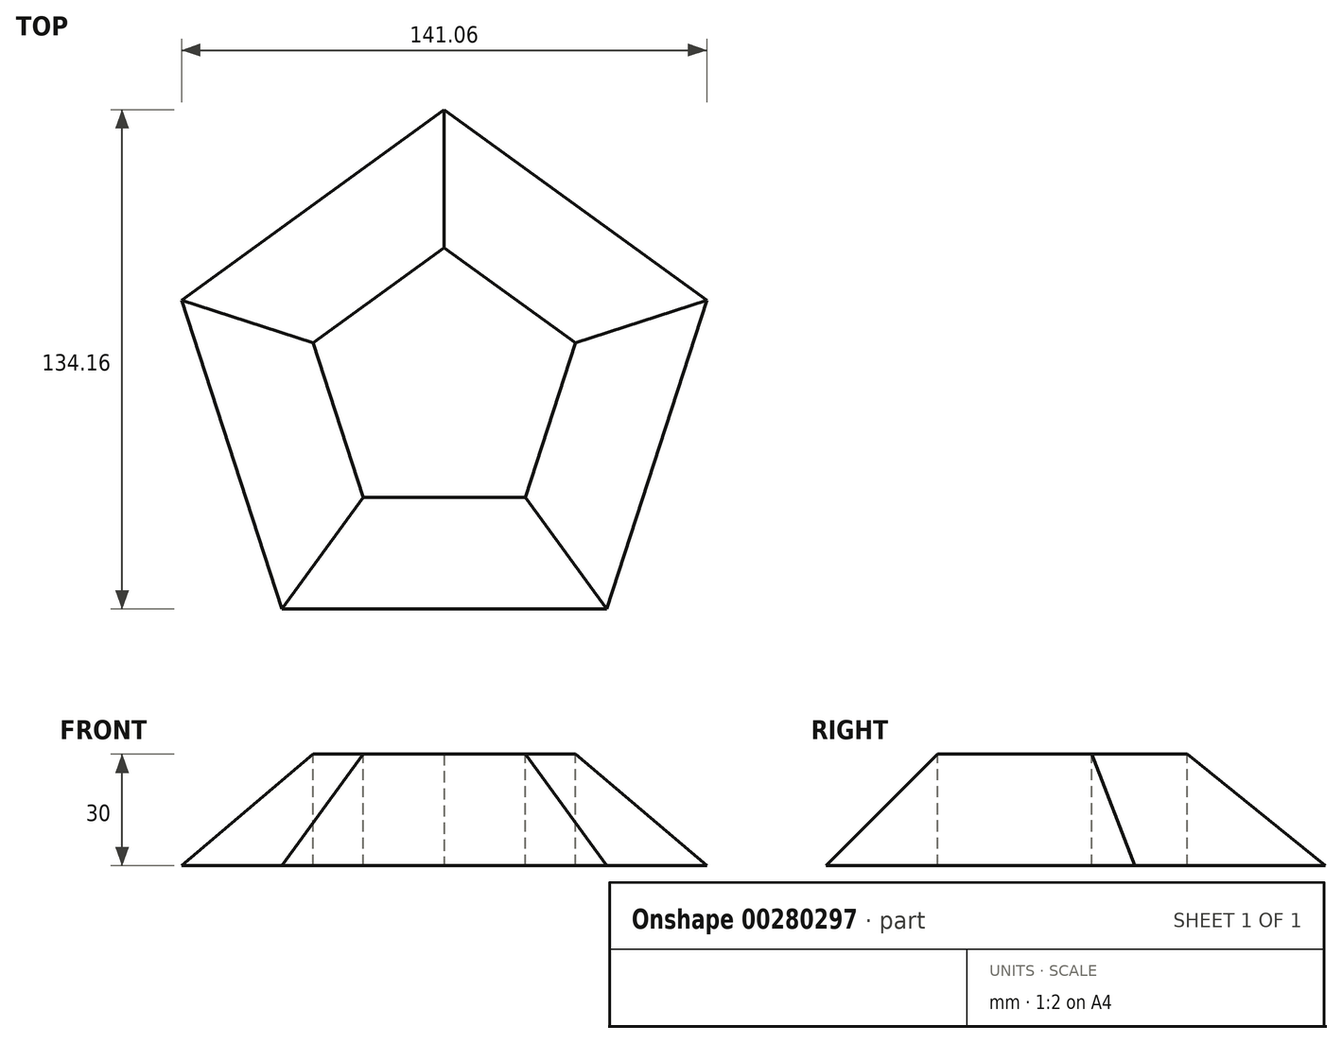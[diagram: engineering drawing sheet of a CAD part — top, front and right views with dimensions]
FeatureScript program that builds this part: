
annotation { "Feature Type Name" : "Feature", "Feature Type Description" : "" }
export const myFeature = defineFeature(function(context is Context, id is Id, definition is map)
    precondition{}
    {
        {
            var Q0;
            Q0=qCreatedBy(makeId("Top.planeOp"),FACE);
            var sketch = newSketch(context, id + "F0", { "sketchPlane" : qUnion([Q0])});
            skCircle(sketch, "E0.cCircle", {"center": v(0, 0) * mm, "radius": 60 * mm, "construction": true});
            skLineSegment(sketch, "E0.0", {"start": v(0, 74.16) * mm, "end": v(70.53, 22.92) * mm});
            skLineSegment(sketch, "E0.1", {"start": v(70.53, 22.92) * mm, "end": v(43.6, -60) * mm});
            skLineSegment(sketch, "E0.2", {"start": v(43.6, -60) * mm, "end": v(-43.6, -60) * mm});
            skLineSegment(sketch, "E0.3", {"start": v(-43.6, -60) * mm, "end": v(-70.53, 22.92) * mm});
            skLineSegment(sketch, "E0.4", {"start": v(-70.53, 22.92) * mm, "end": v(0, 74.16) * mm});
            skPoint(sketch, "E0.0.midPoint", {"position": v(35.27, 48.54) * mm});
            skSolve(sketch);
        }
        {
            var Q0;
            Q0 = qSketchRegion(id + "F0", true);
            extrude(context, id + "F1", {"entities" : qUnion([Q0]), "depth" : 60 * mm, "hasDraft" : true, "draftAngle" : 45 * degree, "draftPullDirection" : true});
        }
        {
            var Q0;
            Q0=qCreatedBy(makeId("Top.planeOp"),FACE);
            cPlane(context, id + "F2", {"entities" : qUnion([Q0]), "cplaneType" : CPlaneType.OFFSET, "offset" : 30 * mm, "width" : 150 * mm, "height" : 150 * mm});
        }
        {
            var Q0;
            Q0=qCreatedBy(id+"F2.planeOp",FACE);
            var sketch = newSketch(context, id + "F3", { "sketchPlane" : qUnion([Q0])});
            skLineSegment(sketch, "E1", {"start": v(-21.8, -30) * mm, "end": v(21.8, -30) * mm});
            skLineSegment(sketch, "E2", {"start": v(-35.27, 11.46) * mm, "end": v(-21.8, -30) * mm});
            skLineSegment(sketch, "E3", {"start": v(21.8, -30) * mm, "end": v(35.27, 11.46) * mm});
            skLineSegment(sketch, "E4", {"start": v(35.27, 11.46) * mm, "end": v(0, 37.08) * mm});
            skLineSegment(sketch, "E5", {"start": v(0, 37.08) * mm, "end": v(-35.27, 11.46) * mm});
            skSolve(sketch);
        }
        {
            var Q0;
            Q0 = qSketchRegion(id + "F3", true);
            extrude(context, id + "F4", {"entities" : qUnion([Q0]), "operationType" : NewBodyOperationType.REMOVE, "endBound" : BoundingType.SYMMETRIC, "oppositeDirection" : true, "depth" : 60 * mm});
        }
    });
